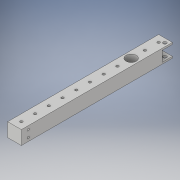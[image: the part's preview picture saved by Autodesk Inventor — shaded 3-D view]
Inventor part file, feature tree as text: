
AUTODESK INVENTOR PART (.ipt)
format: ipt  version: 2018 (Build 220112000, 112)  size: 162,304 bytes
history: native  units: in
note: dims shown in document units (in); Inventor stores cm internally (conversion verified against a paired STEP export)
features: extrude x4, sketch x4
ambient origin geometry x8: Origin, YZ Plane, XZ Plane, XY Plane, X Axis, Y Axis, Z Axis, Center Point
bodies: Solid1 (feature_tree)
feature tree (8):
  extrude  "Extrusion1"  Depth=1.0in
  extrude  "Extrusion2"  Depth=0.1875in
  extrude  "Extrusion3"  Depth=0.5in
  extrude  "Extrusion4"  Depth=0.3937in
  sketch  "Sketch1"  dims[d0=1.0in d1=1.0in]
  sketch  "Sketch2"  dims[d2=11.0in d3=0.0in d4=0.1875in]
  sketch  "Sketch3"  dims[d5=0.5in d6=0.5in]
  sketch  "Sketch4"  dims[d7=4.3307in d9=1.0in d10=0.3937in d12=1.0in d14=0.75in d15=11.0in d16=0.0in d17=0.0in d18=0.75in d19=0.125in d20=0.125in d21=11.0in d22=0.0in d25=0.25in d27=0.25in d28=2.2in d29=0.163in d30=0.5in d31=0.163in d32=0.5in d34=0.5in d35=1.0in d36=0.0in d37=0.252in]
